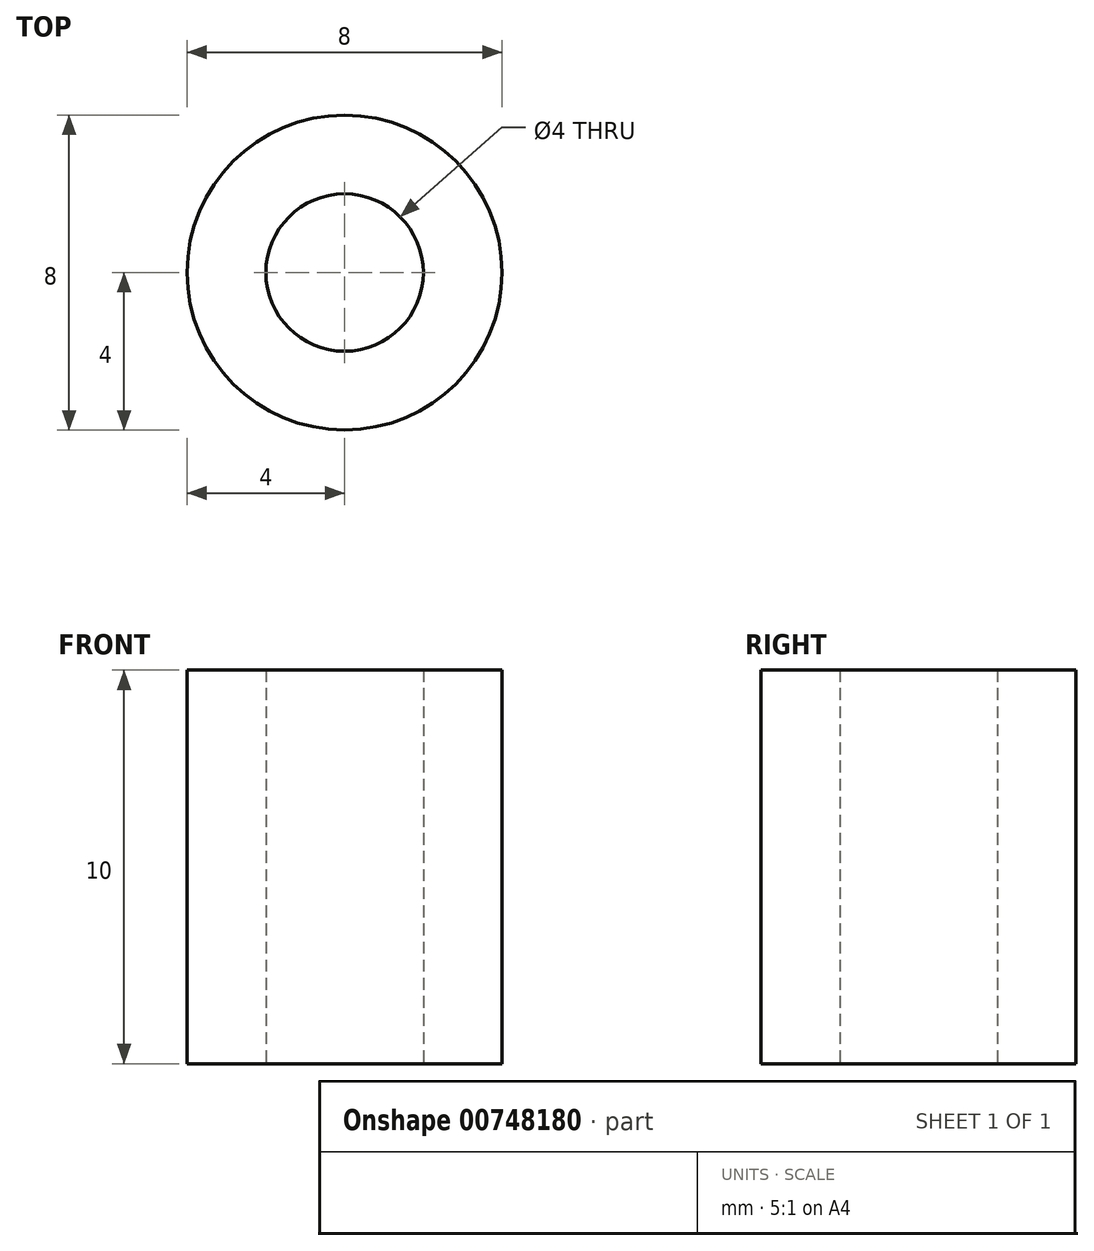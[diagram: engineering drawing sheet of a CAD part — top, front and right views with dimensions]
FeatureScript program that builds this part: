
annotation { "Feature Type Name" : "Feature", "Feature Type Description" : "" }
export const myFeature = defineFeature(function(context is Context, id is Id, definition is map)
    precondition{}
    {
        {
            var Q0;
            Q0=qCreatedBy(makeId("Top.planeOp"),FACE);
            var sketch = newSketch(context, id + "F0", { "sketchPlane" : qUnion([Q0])});
            skCircle(sketch, "E0", {"center": v(0, 0) * mm, "radius": 2 * mm});
            skCircle(sketch, "E1", {"center": v(0, 0) * mm, "radius": 4 * mm});
            skSolve(sketch);
        }
        {
            var Q0;
            Q0=makeQuery(id+"F0.imprint","IMPRINT",FACE,{"disambiguationData":[TD([[makeQuery(id+"F0.imprint","IMPRINT",EDGE,{"derivedFrom":sQuery(id+"F0.wireOp",EDGE,"E0")}),-1.0]])]});
            extrude(context, id + "F1", {"entities" : qUnion([Q0]), "depth" : 10 * mm, "offsetDistance" : 25 * mm});
        }
    });
